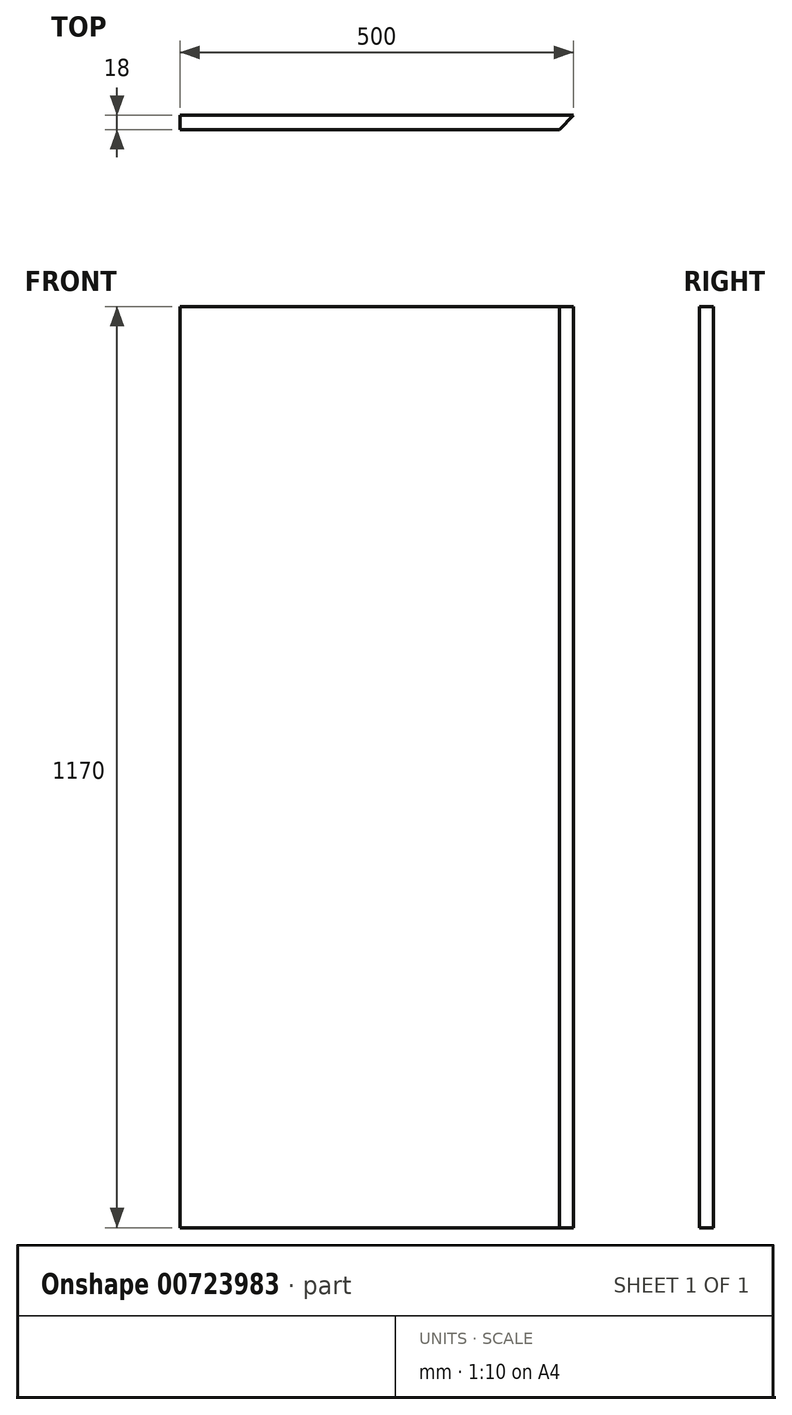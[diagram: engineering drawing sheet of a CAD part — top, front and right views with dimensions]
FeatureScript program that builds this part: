
annotation { "Feature Type Name" : "Feature", "Feature Type Description" : "" }
export const myFeature = defineFeature(function(context is Context, id is Id, definition is map)
    precondition{}
    {
        {
            var Q0;
            Q0=qCreatedBy(makeId("Front.planeOp"),FACE);
            var sketch = newSketch(context, id + "F0", { "sketchPlane" : qUnion([Q0])});
            skLineSegment(sketch, "E0.bottom", {"start": v(-250, 585) * mm, "end": v(250, 585) * mm});
            skLineSegment(sketch, "E0.top", {"start": v(-250, -585) * mm, "end": v(250, -585) * mm});
            skLineSegment(sketch, "E0.left", {"start": v(-250, 585) * mm, "end": v(-250, -585) * mm});
            skLineSegment(sketch, "E0.right", {"start": v(250, 585) * mm, "end": v(250, -585) * mm});
            skLineSegment(sketch, "E1", {"start": v(-250, 585) * mm, "end": v(250, -585) * mm, "construction": true});
            skLineSegment(sketch, "E2", {"start": v(250, 585) * mm, "end": v(-250, -585) * mm, "construction": true});
            skSolve(sketch);
        }
        {
            var Q0;
            Q0=qSketchRegion(id+"F0",true);
            extrude(context, id + "F1", {"entities" : qUnion([Q0]), "depth" : 18 * mm, "offsetDistance" : 25 * mm});
        }
        {
            var Q0;
            Q0=makeQuery(id+"F1.opExtrude","CAP_EDGE",EDGE,{"disambiguationData":[OSD([sQuery(id+"F0.wireOp",EDGE,"E0.right")])],"isStart":false});
            chamfer(context, id + "F2", {"entities" : qUnion([Q0]), "width" : 18 * mm, "tangentPropagation" : true});
        }
    });
